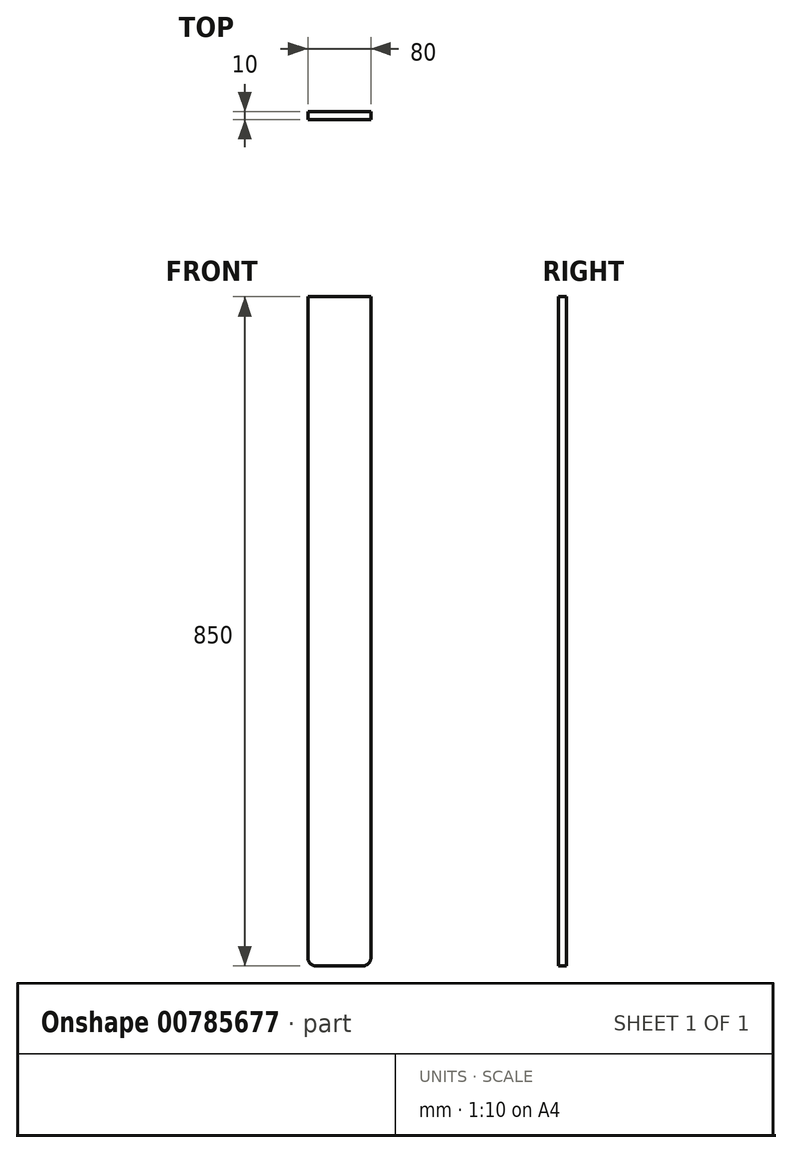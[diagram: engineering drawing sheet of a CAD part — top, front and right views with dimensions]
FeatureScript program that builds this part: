
annotation { "Feature Type Name" : "Feature", "Feature Type Description" : "" }
export const myFeature = defineFeature(function(context is Context, id is Id, definition is map)
    precondition{}
    {
        {
            var Q0;
            Q0=qCreatedBy(makeId("Front.planeOp"),FACE);
            var sketch = newSketch(context, id + "F0", { "sketchPlane" : qUnion([Q0])});
            skLineSegment(sketch, "E0.bottom", {"start": v(-126.94, -500.48) * mm, "end": v(-206.94, -500.48) * mm});
            skLineSegment(sketch, "E0.top", {"start": v(-126.94, 349.52) * mm, "end": v(-206.94, 349.52) * mm});
            skLineSegment(sketch, "E0.left", {"start": v(-126.94, -500.48) * mm, "end": v(-126.94, 349.52) * mm});
            skLineSegment(sketch, "E0.right", {"start": v(-206.94, -500.48) * mm, "end": v(-206.94, 349.52) * mm});
            skPoint(sketch, "E0.middle", {"position": v(-166.94, -75.48) * mm});
            skSolve(sketch);
        }
        {
            var Q0;
            Q0 = qSketchRegion(id + "F0", true);
            extrude(context, id + "F1", {"entities" : qUnion([Q0]), "depth" : 10 * mm, "offsetDistance" : 25 * mm});
        }
        {
            var Q0;
            Q0=makeQuery(id+"F1.opExtrude","SWEPT_EDGE",EDGE,{"disambiguationData":[OSD([sQuery(id+"F0.wireOp",EDGE,"E0.bottom"),sQuery(id+"F0.wireOp",EDGE,"E0.left")])]});
            var Q1;
            Q1=makeQuery(id+"F1.opExtrude","SWEPT_EDGE",EDGE,{"disambiguationData":[OSD([sQuery(id+"F0.wireOp",EDGE,"E0.bottom"),sQuery(id+"F0.wireOp",EDGE,"E0.right")])]});
            fillet(context, id + "F2", {"entities" : qUnion([Q0, Q1]), "radius" : 10 * mm, "tangentPropagation" : true, "allowEdgeOverflow" : false});
        }
    });
